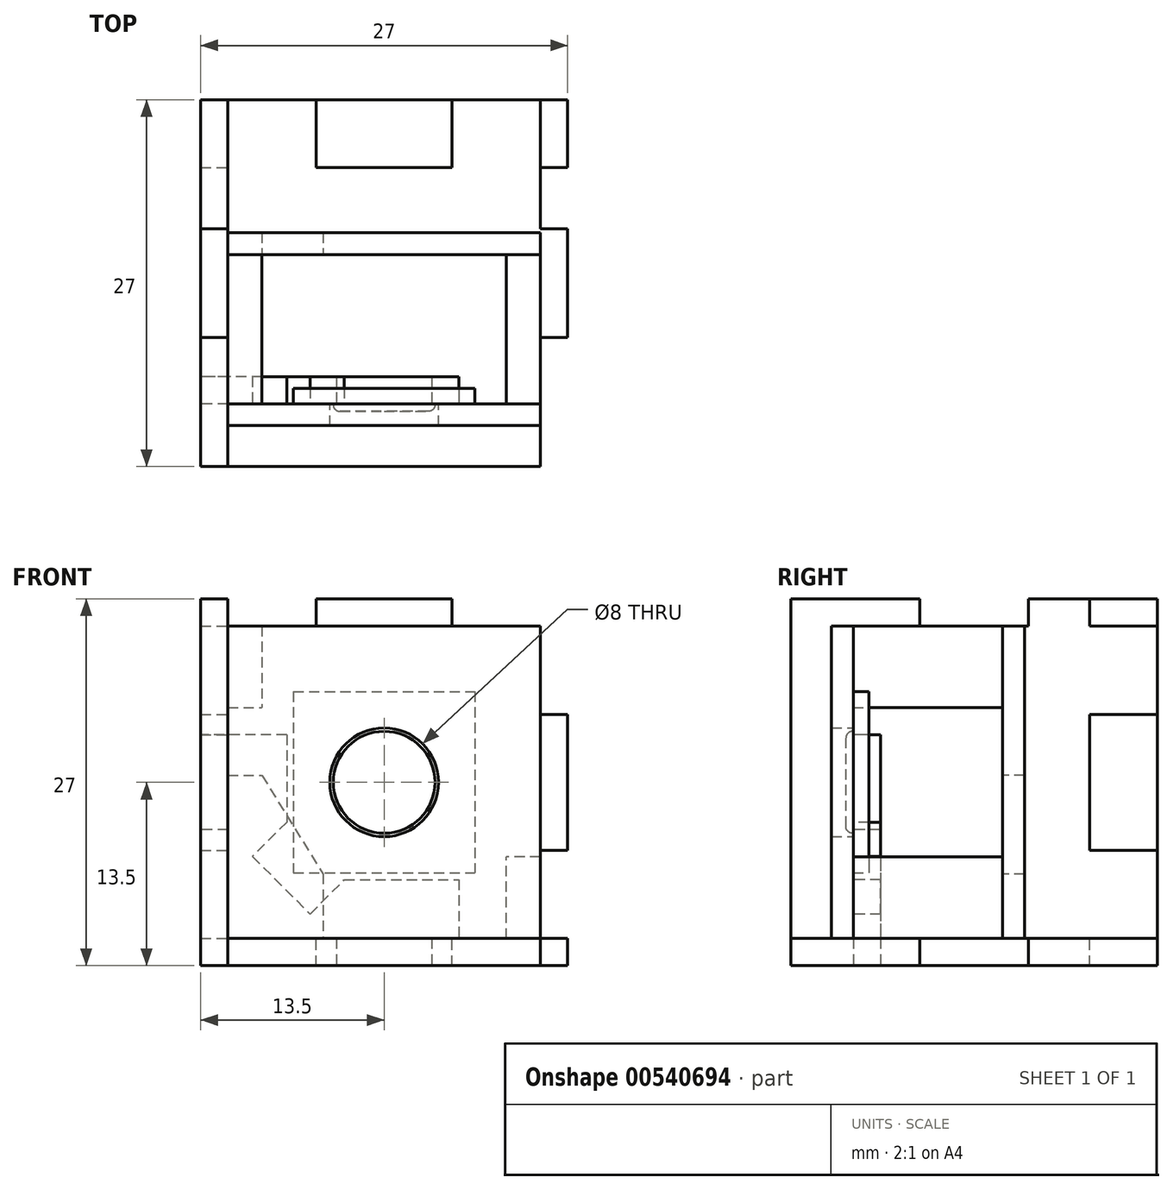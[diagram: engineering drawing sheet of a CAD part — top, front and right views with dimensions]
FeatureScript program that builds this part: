
annotation { "Feature Type Name" : "Feature", "Feature Type Description" : "" }
export const myFeature = defineFeature(function(context is Context, id is Id, definition is map)
    precondition{}
    {
        {
            var Q0;
            Q0=qCreatedBy(makeId("Front.planeOp"),FACE);
            var sketch = newSketch(context, id + "F0", { "sketchPlane" : qUnion([Q0])});
            skLineSegment(sketch, "E0.bottom", {"start": v(-6.68, 6.68) * mm, "end": v(6.68, 6.68) * mm});
            skLineSegment(sketch, "E0.top", {"start": v(-6.68, -6.68) * mm, "end": v(6.68, -6.68) * mm});
            skLineSegment(sketch, "E0.left", {"start": v(-6.68, 6.68) * mm, "end": v(-6.68, -6.68) * mm});
            skLineSegment(sketch, "E0.right", {"start": v(6.68, 6.68) * mm, "end": v(6.67, -6.68) * mm});
            skPoint(sketch, "E0.middle", {"position": v(0, 0) * mm});
            skSolve(sketch);
        }
        {
            var Q0;
            Q0=qSketchRegion(id+"F0",true);
            extrude(context, id + "F1", {"entities" : qUnion([Q0]), "depth" : 1.15 * mm});
        }
        {
            var Q0;
            Q0=makeQuery(id+"F1.opExtrude","CAP_FACE",FACE,{"disambiguationData":[OSD([sQuery(id+"F0.wireOp",EDGE,"E0.bottom"),sQuery(id+"F0.wireOp",EDGE,"E0.top"),sQuery(id+"F0.wireOp",EDGE,"E0.left"),sQuery(id+"F0.wireOp",EDGE,"E0.right")])],"isStart":false});
            var sketch = newSketch(context, id + "F2", { "sketchPlane" : qUnion([Q0])});
            skCircle(sketch, "E1", {"center": v(0, 0) * mm, "radius": 3.75 * mm});
            skSolve(sketch);
        }
        {
            var Q0;
            Q0=qSketchRegion(id+"F2",true);
            extrude(context, id + "F3", {"entities" : qUnion([Q0]), "operationType" : NewBodyOperationType.ADD, "depth" : 0.55 * mm});
        }
        {
            var Q0;
            Q0=makeQuery(id+"F3.opExtrude","CAP_FACE",FACE,{"disambiguationData":[OSD([sQuery(id+"F2.wireOp",EDGE,"E1")])],"isStart":false});
            fillet(context, id + "F4", {"entities" : qUnion([Q0]), "radius" : 0.5 * mm, "tangentPropagation" : true, "allowEdgeOverflow" : false});
        }
        {
            var Q0;
            Q0=makeQuery(id+"F1.opExtrude","CAP_FACE",FACE,{"disambiguationData":[OSD([sQuery(id+"F0.wireOp",EDGE,"E0.bottom"),sQuery(id+"F0.wireOp",EDGE,"E0.top"),sQuery(id+"F0.wireOp",EDGE,"E0.left"),sQuery(id+"F0.wireOp",EDGE,"E0.right")])],"isStart":false});
            var sketch = newSketch(context, id + "F5", { "sketchPlane" : qUnion([Q0])});
            skLineSegment(sketch, "E2.bottom", {"start": v(-11.5, 11.5) * mm, "end": v(11.5, 11.5) * mm});
            skLineSegment(sketch, "E2.top", {"start": v(-11.5, -11.5) * mm, "end": v(11.5, -11.5) * mm});
            skLineSegment(sketch, "E2.left", {"start": v(-11.5, 11.5) * mm, "end": v(-11.5, -11.5) * mm});
            skLineSegment(sketch, "E2.right", {"start": v(11.5, 11.5) * mm, "end": v(11.5, -11.5) * mm});
            skPoint(sketch, "E2.middle", {"position": v(0, 0) * mm});
            skCircle(sketch, "E3", {"center": v(0, 0) * mm, "radius": 4 * mm});
            skSolve(sketch);
        }
        {
            var Q0;
            Q0=qSketchRegion(id+"F5",true);
            extrude(context, id + "F6", {"entities" : qUnion([Q0]), "depth" : 1.6 * mm});
        }
        {
            var Q0;
            Q0=makeQuery(id+"F6.opExtrude","CAP_FACE",FACE,{"disambiguationData":[OSD([sQuery(id+"F5.wireOp",EDGE,"E2.bottom"),sQuery(id+"F5.wireOp",EDGE,"E2.top"),sQuery(id+"F5.wireOp",EDGE,"E2.left"),sQuery(id+"F5.wireOp",EDGE,"E2.right"),sQuery(id+"F5.wireOp",EDGE,"E3")])],"isStart":true});
            cPlane(context, id + "F7", {"entities" : qUnion([Q0]), "cplaneType" : CPlaneType.OFFSET, "offset" : 11 * mm, "width" : 150 * mm, "height" : 150 * mm});
        }
        {
            var Q0;
            Q0=qCreatedBy(id+"F7.planeOp",FACE);
            var sketch = newSketch(context, id + "F8", { "sketchPlane" : qUnion([Q0])});
            skLineSegment(sketch, "E4.bottom", {"start": v(11.5, 11.5) * mm, "end": v(-11.5, 11.5) * mm});
            skLineSegment(sketch, "E4.top", {"start": v(11.5, -11.5) * mm, "end": v(-11.5, -11.5) * mm});
            skLineSegment(sketch, "E4.left", {"start": v(11.5, 11.5) * mm, "end": v(11.5, -11.5) * mm});
            skLineSegment(sketch, "E4.right", {"start": v(-11.5, 11.5) * mm, "end": v(-11.5, -11.5) * mm});
            skPoint(sketch, "E4.middle", {"position": v(0, 0) * mm});
            skLineSegment(sketch, "E5", {"start": v(11.5, 0.5) * mm, "end": v(9, 0.5) * mm});
            skLineSegment(sketch, "E6", {"start": v(9, 0.5) * mm, "end": v(4.5, -6.75) * mm});
            skLineSegment(sketch, "E7", {"start": v(4.5, -6.75) * mm, "end": v(4.5, -11.5) * mm});
            skSolve(sketch);
        }
        {
            var Q0;
            {var subQ1=sQuery(id+"F8.wireOp",EDGE,"E4.bottom");Q0=makeQuery(id+"F8.imprint","IMPRINT",FACE,{"disambiguationData":[TD([[makeQuery(id+"F8.imprint","IMPRINT",EDGE,{"derivedFrom":subQ1}),1.0]])]});}
            extrude(context, id + "F9", {"entities" : qUnion([Q0]), "depth" : 1.6 * mm});
        }
        {
            var Q0;
            Q0=makeQuery(id+"F9.opExtrude","CAP_FACE",FACE,{"disambiguationData":[OSD([sQuery(id+"F8.wireOp",EDGE,"E4.bottom"),sQuery(id+"F8.wireOp",EDGE,"E4.top"),sQuery(id+"F8.wireOp",EDGE,"E4.left"),sQuery(id+"F8.wireOp",EDGE,"E4.right"),sQuery(id+"F8.wireOp",EDGE,"E5"),sQuery(id+"F8.wireOp",EDGE,"E6"),sQuery(id+"F8.wireOp",EDGE,"E7")])],"isStart":true});
            var sketch = newSketch(context, id + "F10", { "sketchPlane" : qUnion([Q0])});
            skLineSegment(sketch, "E8.bottom", {"start": v(-11.5, 11.5) * mm, "end": v(-9, 11.5) * mm});
            skLineSegment(sketch, "E8.top", {"start": v(-11.5, 5.5) * mm, "end": v(-9, 5.5) * mm});
            skLineSegment(sketch, "E8.left", {"start": v(-11.5, 11.5) * mm, "end": v(-11.5, 5.5) * mm});
            skLineSegment(sketch, "E8.right", {"start": v(-9, 11.5) * mm, "end": v(-9, 5.5) * mm});
            skLineSegment(sketch, "E9.bottom", {"start": v(11.5, -11.5) * mm, "end": v(9, -11.5) * mm});
            skLineSegment(sketch, "E9.top", {"start": v(11.5, -5.5) * mm, "end": v(9, -5.5) * mm});
            skLineSegment(sketch, "E9.left", {"start": v(11.5, -11.5) * mm, "end": v(11.5, -5.5) * mm});
            skLineSegment(sketch, "E9.right", {"start": v(9, -11.5) * mm, "end": v(9, -5.5) * mm});
            skSolve(sketch);
        }
        {
            var Q0;
            Q0=qSketchRegion(id+"F10",true);
            extrude(context, id + "F11", {"entities" : qUnion([Q0]), "endBound" : BoundingType.UP_TO_NEXT, "depth" : 25 * mm});
        }
        {
            var Q0;
            Q0=makeQuery(id+"F6.opExtrude","CAP_FACE",FACE,{"disambiguationData":[OSD([sQuery(id+"F5.wireOp",EDGE,"E2.bottom"),sQuery(id+"F5.wireOp",EDGE,"E2.top"),sQuery(id+"F5.wireOp",EDGE,"E2.left"),sQuery(id+"F5.wireOp",EDGE,"E2.right"),sQuery(id+"F5.wireOp",EDGE,"E3")])],"isStart":true});
            var sketch = newSketch(context, id + "F12", { "sketchPlane" : qUnion([Q0])});
            skPoint(sketch, "E10.middle", {"position": v(0, 0) * mm});
            skLineSegment(sketch, "E11.bottom", {"start": v(5.46, -9) * mm, "end": v(9, -5.45) * mm, "construction": true});
            skLineSegment(sketch, "E11.top", {"start": v(1.92, -5.46) * mm, "end": v(5.46, -1.92) * mm, "construction": true});
            skLineSegment(sketch, "E11.left", {"start": v(5.46, -9) * mm, "end": v(1.92, -5.46) * mm, "construction": true});
            skLineSegment(sketch, "E11.right", {"start": v(9, -5.46) * mm, "end": v(5.46, -1.92) * mm, "construction": true});
            skPoint(sketch, "E11.middle", {"position": v(5.46, -5.46) * mm});
            skLineSegment(sketch, "E12", {"start": v(5.46, -5.46) * mm, "end": v(5.46, -1.92) * mm, "construction": true});
            skLineSegment(sketch, "E13.bottom", {"start": v(11.5, -3.5) * mm, "end": v(13.5, -3.5) * mm});
            skLineSegment(sketch, "E13.top", {"start": v(11.5, 3.5) * mm, "end": v(13.5, 3.5) * mm});
            skLineSegment(sketch, "E13.left", {"start": v(11.5, -3.5) * mm, "end": v(11.5, 3.5) * mm});
            skLineSegment(sketch, "E13.right", {"start": v(13.5, -3.5) * mm, "end": v(13.5, 3.5) * mm});
            skPoint(sketch, "E13.middle", {"position": v(12.5, 0) * mm});
            skLineSegment(sketch, "E14.bottom", {"start": v(3.5, -11.5) * mm, "end": v(-3.5, -11.5) * mm});
            skLineSegment(sketch, "E14.top", {"start": v(3.5, -13.5) * mm, "end": v(-3.5, -13.5) * mm});
            skLineSegment(sketch, "E14.left", {"start": v(3.5, -11.5) * mm, "end": v(3.5, -13.5) * mm});
            skLineSegment(sketch, "E14.right", {"start": v(-3.5, -11.5) * mm, "end": v(-3.5, -13.5) * mm});
            skPoint(sketch, "E14.middle", {"position": v(0, -12.5) * mm});
            skLineSegment(sketch, "E15", {"start": v(11.5, -3.5) * mm, "end": v(11.5, -11.5) * mm});
            skLineSegment(sketch, "E16", {"start": v(11.5, -11.5) * mm, "end": v(3.5, -11.5) * mm});
            skLineSegment(sketch, "E17", {"start": v(11.5, 3.5) * mm, "end": v(7.17, 3.5) * mm});
            skLineSegment(sketch, "E18", {"start": v(7.17, 3.5) * mm, "end": v(7.18, -2.93) * mm});
            skLineSegment(sketch, "E19", {"start": v(7.18, -2.93) * mm, "end": v(9.7, -5.46) * mm});
            skLineSegment(sketch, "E20", {"start": v(9.7, -5.46) * mm, "end": v(5.46, -9.7) * mm});
            skLineSegment(sketch, "E21", {"start": v(5.46, -9.7) * mm, "end": v(2.93, -7.18) * mm});
            skLineSegment(sketch, "E22", {"start": v(2.93, -7.18) * mm, "end": v(-5.5, -7.18) * mm});
            skLineSegment(sketch, "E23", {"start": v(-5.5, -7.18) * mm, "end": v(-5.5, -11.5) * mm});
            skLineSegment(sketch, "E24", {"start": v(-5.5, -11.5) * mm, "end": v(-3.5, -11.5) * mm});
            skLineSegment(sketch, "E25", {"start": v(7.58, -7.58) * mm, "end": v(0, 0) * mm, "construction": true});
            skSolve(sketch);
        }
        {
            var Q0;
            Q0=qSketchRegion(id+"F12",true);
            extrude(context, id + "F13", {"entities" : qUnion([Q0]), "depth" : 2 * mm});
        }
        {
            var Q0;
            Q0=makeQuery(id+"F13.opExtrude","SWEPT_FACE",FACE,{"disambiguationData":[OSD([sQuery(id+"F12.wireOp",EDGE,"E16")])]});
            var sketch = newSketch(context, id + "F14", { "sketchPlane" : qUnion([Q0])});
            skLineSegment(sketch, "E26.bottom", {"start": v(-11.5, 5.75) * mm, "end": v(11.5, 5.75) * mm});
            skLineSegment(sketch, "E26.top", {"start": v(-11.5, -21.25) * mm, "end": v(11.5, -21.25) * mm});
            skLineSegment(sketch, "E26.left", {"start": v(-11.5, 5.75) * mm, "end": v(-11.5, -21.25) * mm});
            skLineSegment(sketch, "E26.right", {"start": v(11.5, 5.75) * mm, "end": v(11.5, -21.25) * mm});
            skPoint(sketch, "E26.middle", {"position": v(0, -7.75) * mm});
            skLineSegment(sketch, "E27.0", {"start": v(-3.5, 1.15) * mm, "end": v(3.5, 1.15) * mm});
            skLineSegment(sketch, "E27.1", {"start": v(-3.5, -0.85) * mm, "end": v(-3.5, 1.15) * mm});
            skLineSegment(sketch, "E27.2", {"start": v(-3.5, -0.85) * mm, "end": v(3.5, -0.85) * mm});
            skLineSegment(sketch, "E27.3", {"start": v(3.5, -0.85) * mm, "end": v(3.5, 1.15) * mm});
            skLineSegment(sketch, "E28.bottom", {"start": v(5, -21.25) * mm, "end": v(-5, -21.25) * mm});
            skLineSegment(sketch, "E28.top", {"start": v(5, -16.25) * mm, "end": v(-5, -16.25) * mm});
            skLineSegment(sketch, "E28.left", {"start": v(5, -21.25) * mm, "end": v(5, -16.25) * mm});
            skLineSegment(sketch, "E28.right", {"start": v(-5, -21.25) * mm, "end": v(-5, -16.25) * mm});
            skPoint(sketch, "E28.middle", {"position": v(0, -18.75) * mm});
            skLineSegment(sketch, "E29.bottom", {"start": v(-11.5, -3.75) * mm, "end": v(-13.5, -3.75) * mm});
            skLineSegment(sketch, "E29.top", {"start": v(-11.5, -11.75) * mm, "end": v(-13.5, -11.75) * mm});
            skLineSegment(sketch, "E29.left", {"start": v(-11.5, -3.75) * mm, "end": v(-11.5, -11.75) * mm});
            skLineSegment(sketch, "E29.right", {"start": v(-13.5, -3.75) * mm, "end": v(-13.5, -11.75) * mm});
            skPoint(sketch, "E29.middle", {"position": v(-12.5, -7.75) * mm});
            skLineSegment(sketch, "E30", {"start": v(0, -7.75) * mm, "end": v(0, -3.1) * mm, "construction": true});
            skLineSegment(sketch, "E31.MirrorCS", {"start": v(11.5, -3.75) * mm, "end": v(13.5, -3.75) * mm});
            skLineSegment(sketch, "E32.MirrorCS", {"start": v(13.5, -3.75) * mm, "end": v(13.5, -11.75) * mm});
            skLineSegment(sketch, "E33.MirrorCS", {"start": v(11.5, -11.75) * mm, "end": v(13.5, -11.75) * mm});
            skSolve(sketch);
        }
        {
            var Q0;
            Q0=makeQuery(id+"F14.imprint","IMPRINT",FACE,{"disambiguationData":[TD([[makeQuery(id+"F14.imprint","IMPRINT",EDGE,{"derivedFrom":sQuery(id+"F14.wireOp",EDGE,"E27.1")}),1.0]])]});
            var Q1;
            {var subQ6=sQuery(id+"F14.wireOp",EDGE,"E26.bottom");Q1=makeQuery(id+"F14.imprint","IMPRINT",FACE,{"disambiguationData":[TD([[makeQuery(id+"F14.imprint","IMPRINT",EDGE,{"derivedFrom":subQ6}),-1.0]])]});}
            var Q2;
            Q2=makeQuery(id+"F14.imprint","IMPRINT",FACE,{"disambiguationData":[TD([[makeQuery(id+"F14.imprint","IMPRINT",EDGE,{"derivedFrom":sQuery(id+"F14.wireOp",EDGE,"E29.bottom")}),1.0]])]});
            var Q3;
            {var subQ0=sQuery(id+"F14.wireOp",EDGE,"E31.MirrorCS");Q3=makeQuery(id+"F14.imprint","IMPRINT",FACE,{"disambiguationData":[TD([[makeQuery(id+"F14.imprint","IMPRINT",EDGE,{"derivedFrom":subQ0}),-1.0]])]});}
            extrude(context, id + "F15", {"entities" : qUnion([Q0, Q1, Q2, Q3]), "depth" : 2 * mm});
        }
        {
            var Q0;
            Q0=makeQuery(id+"F13.opExtrude","SWEPT_FACE",FACE,{"disambiguationData":[OSD([sQuery(id+"F12.wireOp",EDGE,"E15")])]});
            var sketch = newSketch(context, id + "F16", { "sketchPlane" : qUnion([Q0])});
            skLineSegment(sketch, "E34.bottom", {"start": v(5.75, -13.5) * mm, "end": v(-21.25, -13.5) * mm});
            skLineSegment(sketch, "E34.top", {"start": v(5.75, 13.5) * mm, "end": v(-21.25, 13.5) * mm});
            skLineSegment(sketch, "E34.left", {"start": v(5.75, -13.5) * mm, "end": v(5.75, 13.5) * mm});
            skLineSegment(sketch, "E34.right", {"start": v(-21.25, -13.5) * mm, "end": v(-21.25, 13.5) * mm});
            skPoint(sketch, "E34.middle", {"position": v(-7.75, 0) * mm});
            skLineSegment(sketch, "E35.0", {"start": v(1.15, -3.5) * mm, "end": v(1.15, 3.5) * mm});
            skLineSegment(sketch, "E35.1", {"start": v(-0.85, 3.5) * mm, "end": v(1.15, 3.5) * mm});
            skLineSegment(sketch, "E35.2", {"start": v(-0.85, -3.5) * mm, "end": v(-0.85, 3.5) * mm});
            skLineSegment(sketch, "E35.3", {"start": v(-0.85, -3.5) * mm, "end": v(1.15, -3.5) * mm});
            skLineSegment(sketch, "E36.bottom", {"start": v(-21.25, -5) * mm, "end": v(-16.25, -5) * mm});
            skLineSegment(sketch, "E36.top", {"start": v(-21.25, 5) * mm, "end": v(-16.25, 5) * mm});
            skLineSegment(sketch, "E36.left", {"start": v(-21.25, -5) * mm, "end": v(-21.25, 5) * mm});
            skLineSegment(sketch, "E36.right", {"start": v(-16.25, -5) * mm, "end": v(-16.25, 5) * mm});
            skPoint(sketch, "E36.middle", {"position": v(-18.75, 0) * mm});
            skLineSegment(sketch, "E37.0", {"start": v(-11.75, -13.5) * mm, "end": v(-11.75, -11.5) * mm});
            skLineSegment(sketch, "E37.1", {"start": v(-3.75, -11.5) * mm, "end": v(-11.75, -11.5) * mm});
            skLineSegment(sketch, "E37.2", {"start": v(-3.75, -13.5) * mm, "end": v(-3.75, -11.5) * mm});
            skLineSegment(sketch, "E38", {"start": v(-7.75, 0) * mm, "end": v(-2.75, 0) * mm, "construction": true});
            skLineSegment(sketch, "E39.MirrorCS", {"start": v(-3.75, 13.5) * mm, "end": v(-3.75, 11.5) * mm});
            skLineSegment(sketch, "E40.MirrorCS", {"start": v(-3.75, 11.5) * mm, "end": v(-11.75, 11.5) * mm});
            skLineSegment(sketch, "E41.MirrorCS", {"start": v(-11.75, 13.5) * mm, "end": v(-11.75, 11.5) * mm});
            skSolve(sketch);
        }
        {
            var Q0;
            Q0=makeQuery(id+"F16.imprint","IMPRINT",FACE,{"disambiguationData":[TD([[makeQuery(id+"F16.imprint","IMPRINT",EDGE,{"derivedFrom":sQuery(id+"F16.wireOp",EDGE,"E35.3")}),-1.0]])]});
            var Q1;
            {var subQ5=sQuery(id+"F16.wireOp",EDGE,"E34.bottom");Q1=makeQuery(id+"F16.imprint","IMPRINT",FACE,{"disambiguationData":[TD([[makeQuery(id+"F16.imprint","IMPRINT",EDGE,{"derivedFrom":subQ5}),-1.0]])]});}
            extrude(context, id + "F17", {"entities" : qUnion([Q0, Q1]), "depth" : 2 * mm});
        }
        {
            var Q0;
            Q0=makeQuery(id+"F15.opExtrude","SWEPT_FACE",FACE,{"disambiguationData":[OSD([sQuery(id+"F14.wireOp",EDGE,"E28.top")])]});
            var sketch = newSketch(context, id + "F18", { "sketchPlane" : qUnion([Q0])});
            skLineSegment(sketch, "E42.bottom", {"start": v(-11.5, 11.5) * mm, "end": v(11.5, 11.5) * mm});
            skLineSegment(sketch, "E42.top", {"start": v(-11.5, -11.5) * mm, "end": v(11.5, -11.5) * mm});
            skLineSegment(sketch, "E42.left", {"start": v(-11.5, 11.5) * mm, "end": v(-11.5, -11.5) * mm});
            skLineSegment(sketch, "E42.right", {"start": v(11.5, 11.5) * mm, "end": v(11.5, -11.5) * mm});
            skPoint(sketch, "E42.middle", {"position": v(0, 0) * mm});
            skLineSegment(sketch, "E43.bottom", {"start": v(-5, -13.5) * mm, "end": v(5, -13.5) * mm});
            skLineSegment(sketch, "E43.top", {"start": v(-5, -11.5) * mm, "end": v(5, -11.5) * mm});
            skLineSegment(sketch, "E43.left", {"start": v(-5, -13.5) * mm, "end": v(-5, -11.5) * mm});
            skLineSegment(sketch, "E43.right", {"start": v(5, -13.5) * mm, "end": v(5, -11.5) * mm});
            skLineSegment(sketch, "E44.1.1", {"start": v(13.5, -5) * mm, "end": v(11.5, -5) * mm});
            skLineSegment(sketch, "E44.1.2", {"start": v(13.5, -5) * mm, "end": v(13.5, 5) * mm});
            skLineSegment(sketch, "E44.1.3", {"start": v(13.5, 5) * mm, "end": v(11.5, 5) * mm});
            skLineSegment(sketch, "E44.2.1", {"start": v(5, 13.5) * mm, "end": v(5, 11.5) * mm});
            skLineSegment(sketch, "E44.2.2", {"start": v(5, 13.5) * mm, "end": v(-5, 13.5) * mm});
            skLineSegment(sketch, "E44.2.3", {"start": v(-5, 13.5) * mm, "end": v(-5, 11.5) * mm});
            skLineSegment(sketch, "E44.3.1", {"start": v(-13.5, 5) * mm, "end": v(-11.5, 5) * mm});
            skLineSegment(sketch, "E44.3.2", {"start": v(-13.5, 5) * mm, "end": v(-13.5, -5) * mm});
            skLineSegment(sketch, "E44.3.3", {"start": v(-13.5, -5) * mm, "end": v(-11.5, -5) * mm});
            skCircle(sketch, "E45", {"center": v(0, 0) * mm, "radius": 2.5 * mm});
            skCircle(sketch, "E46", {"center": v(-7, -7) * mm, "radius": 3 * mm});
            skLineSegment(sketch, "E47", {"start": v(-11.5, -11.5) * mm, "end": v(11.5, 11.5) * mm, "construction": true});
            skCircle(sketch, "E48", {"center": v(7, 7) * mm, "radius": 3 * mm});
            skSolve(sketch);
        }
        {
            var Q0;
            {var subQ11=sQuery(id+"F18.wireOp",EDGE,"E43.top");Q0=makeQuery(id+"F18.imprint","IMPRINT",FACE,{"disambiguationData":[TD([[makeQuery(id+"F18.imprint","IMPRINT",EDGE,{"derivedFrom":subQ11}),1.0]])]});}
            var Q1;
            {var subQ0=sQuery(id+"F18.wireOp",EDGE,"E44.3.1");Q1=makeQuery(id+"F18.imprint","IMPRINT",FACE,{"disambiguationData":[TD([[makeQuery(id+"F18.imprint","IMPRINT",EDGE,{"derivedFrom":subQ0}),-1.0]])]});}
            var Q2;
            Q2=makeQuery(id+"F18.imprint","IMPRINT",FACE,{"disambiguationData":[TD([[makeQuery(id+"F18.imprint","IMPRINT",EDGE,{"derivedFrom":sQuery(id+"F18.wireOp",EDGE,"E43.bottom")}),1.0]])]});
            var Q3;
            {var subQ0=sQuery(id+"F18.wireOp",EDGE,"E44.2.1");Q3=makeQuery(id+"F18.imprint","IMPRINT",FACE,{"disambiguationData":[TD([[makeQuery(id+"F18.imprint","IMPRINT",EDGE,{"derivedFrom":subQ0}),-1.0]])]});}
            var Q4;
            {var subQ0=sQuery(id+"F18.wireOp",EDGE,"E44.1.1");Q4=makeQuery(id+"F18.imprint","IMPRINT",FACE,{"disambiguationData":[TD([[makeQuery(id+"F18.imprint","IMPRINT",EDGE,{"derivedFrom":subQ0}),-1.0]])]});}
            extrude(context, id + "F19", {"entities" : qUnion([Q0, Q1, Q2, Q3, Q4]), "depth" : 5 * mm});
        }
    });
